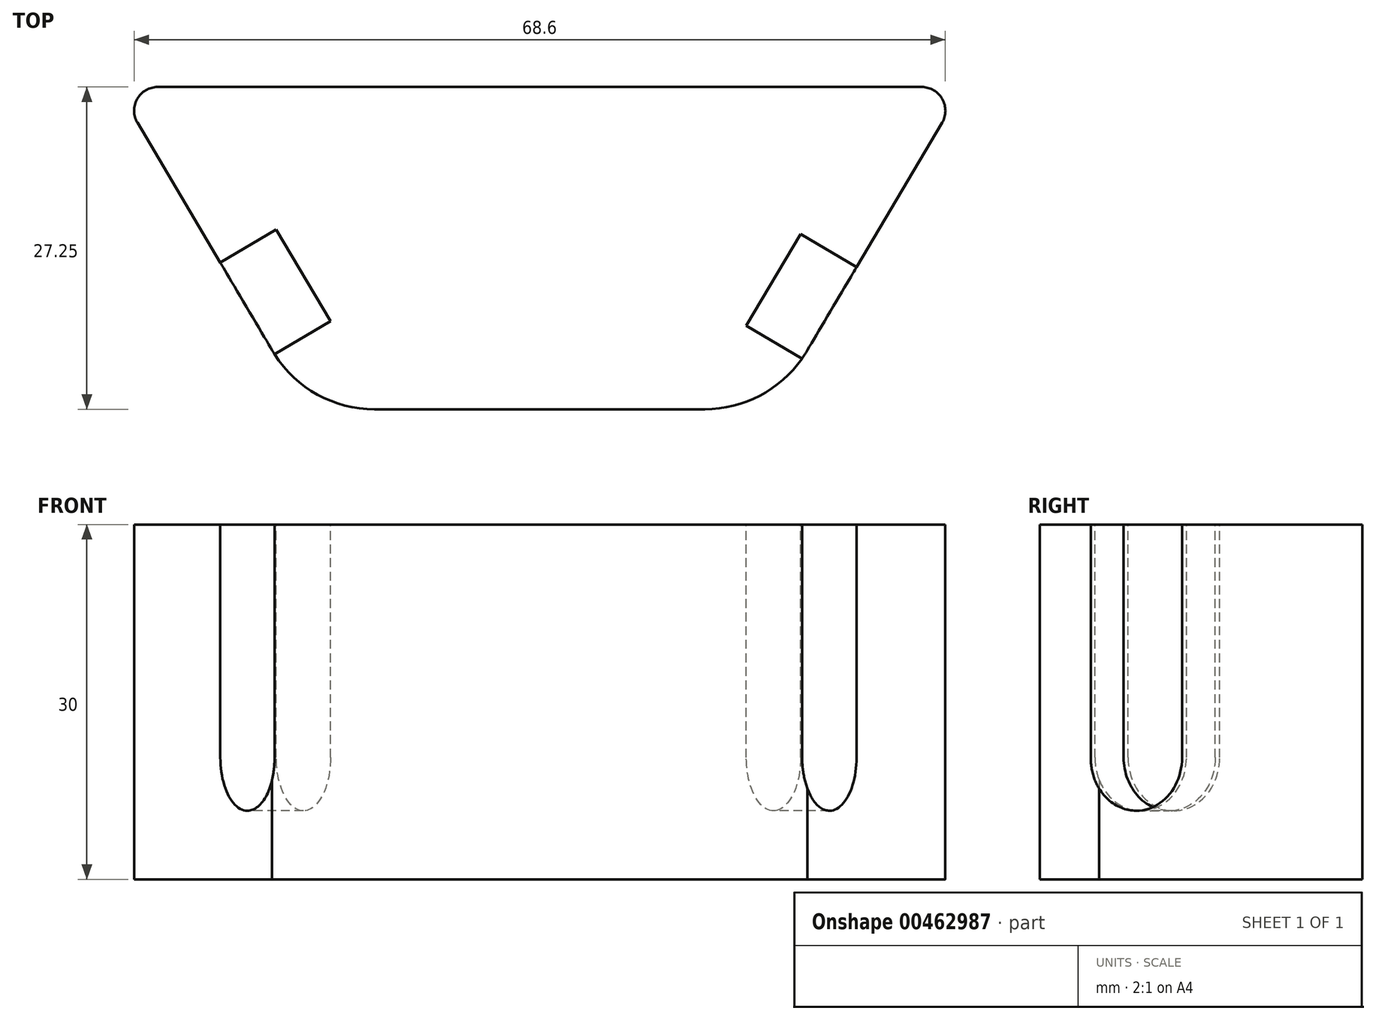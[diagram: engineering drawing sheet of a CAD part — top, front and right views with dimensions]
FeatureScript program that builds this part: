
annotation { "Feature Type Name" : "Feature", "Feature Type Description" : "" }
export const myFeature = defineFeature(function(context is Context, id is Id, definition is map)
    precondition{}
    {
        {
            var Q0;
            Q0=qCreatedBy(makeId("Top.planeOp"),FACE);
            var sketch = newSketch(context, id + "F0", { "sketchPlane" : qUnion([Q0])});
            skLineSegment(sketch, "E0", {"start": v(14.22, 4.24) * mm, "end": v(-13.72, 4.24) * mm});
            skPoint(sketch, "E1.visualSharp", {"position": v(-20, 4.24) * mm});
            skArc(sketch, "E1.filletArc", {"start": v(-22.38, 9.24) * mm, "mid": v(-18.72, 5.58) * mm, "end": v(-13.72, 4.24) * mm});
            skPoint(sketch, "E2.visualSharp", {"position": v(20, 4.24) * mm});
            skArc(sketch, "E2.filletArc", {"start": v(14.22, 4.24) * mm, "mid": v(19.22, 5.58) * mm, "end": v(22.88, 9.24) * mm});
            skLineSegment(sketch, "E3", {"start": v(32.55, 31.5) * mm, "end": v(-32.05, 31.49) * mm});
            skLineSegment(sketch, "E4.trimOffspring", {"start": v(-33.77, 28.47) * mm, "end": v(-22.38, 9.24) * mm});
            skLineSegment(sketch, "E5.trimOffspring", {"start": v(34.27, 28.47) * mm, "end": v(22.88, 9.24) * mm});
            skArc(sketch, "E6.filletArc", {"start": v(-32.05, 31.49) * mm, "mid": v(-33.8, 30.48) * mm, "end": v(-33.77, 28.47) * mm});
            skPoint(sketch, "E7.visualSharp", {"position": v(36.06, 31.5) * mm});
            skArc(sketch, "E7.filletArc", {"start": v(34.27, 28.47) * mm, "mid": v(34.3, 30.48) * mm, "end": v(32.55, 31.5) * mm});
            skSolve(sketch);
        }
        {
            var Q0;
            Q0 = qSketchRegion(id + "F0", true);
            extrude(context, id + "F1", {"entities" : qUnion([Q0]), "depth" : 30 * mm, "offsetDistance" : 25 * mm});
        }
        {
            var Q0;
            Q0=makeQuery(id+"F1.opExtrude","CAP_FACE",FACE,{"disambiguationData":[OSD([sQuery(id+"F0.wireOp",EDGE,"E0"),sQuery(id+"F0.wireOp",EDGE,"E1.filletArc"),sQuery(id+"F0.wireOp",EDGE,"E2.filletArc"),sQuery(id+"F0.wireOp",EDGE,"E3"),sQuery(id+"F0.wireOp",EDGE,"E4.trimOffspring"),sQuery(id+"F0.wireOp",EDGE,"E5.trimOffspring"),sQuery(id+"F0.wireOp",EDGE,"E6.filletArc"),sQuery(id+"F0.wireOp",EDGE,"E7.filletArc")])],"isStart":false});
            var sketch = newSketch(context, id + "F2", { "sketchPlane" : qUnion([Q0])});
            skPoint(sketch, "E8.visualSharp", {"position": v(-23.46, 4.24) * mm});
            skArc(sketch, "E8.filletArc", {"start": v(-22.38, 9.24) * mm, "mid": v(-22.28, 9.06) * mm, "end": v(-22.17, 8.89) * mm});
            skPoint(sketch, "E9.visualSharp", {"position": v(16.54, 4.24) * mm});
            skArc(sketch, "E9.filletArc", {"start": v(22.43, 8.53) * mm, "mid": v(22.66, 8.88) * mm, "end": v(22.88, 9.24) * mm});
            skLineSegment(sketch, "E10", {"start": v(-17.44, 11.69) * mm, "end": v(-22.03, 19.43) * mm});
            skLineSegment(sketch, "E11", {"start": v(-22.03, 19.43) * mm, "end": v(-26.76, 16.63) * mm});
            skPoint(sketch, "E12", {"position": v(-19.42, 4.24) * mm});
            skLineSegment(sketch, "E13", {"start": v(27.04, 16.26) * mm, "end": v(22.3, 19.06) * mm});
            skLineSegment(sketch, "E14", {"start": v(22.3, 19.06) * mm, "end": v(17.72, 11.32) * mm});
            skLineSegment(sketch, "E15", {"start": v(-17.44, 11.69) * mm, "end": v(-22.17, 8.89) * mm});
            skLineSegment(sketch, "E16", {"start": v(17.72, 11.32) * mm, "end": v(22.43, 8.53) * mm});
            skPoint(sketch, "E17.orphan", {"position": v(-13.72, 4.24) * mm});
            skPoint(sketch, "E18.orphan", {"position": v(14.22, 4.24) * mm});
            skLineSegment(sketch, "E19", {"start": v(22.88, 9.24) * mm, "end": v(27.04, 16.26) * mm});
            skLineSegment(sketch, "E20", {"start": v(-26.76, 16.63) * mm, "end": v(-22.38, 9.24) * mm});
            skSolve(sketch);
        }
        {
            var Q0;
            Q0 = qSketchRegion(id + "F2", true);
            extrude(context, id + "F3", {"entities" : qUnion([Q0]), "operationType" : NewBodyOperationType.REMOVE, "oppositeDirection" : true, "depth" : 24.2 * mm, "offsetDistance" : 25 * mm});
        }
        {
            var Q0;
            Q0=makeQuery(id+"F3.boolean.opBoolean","COPY",EDGE,{"derivedFrom":makeQuery(id+"F3.opExtrude","CAP_EDGE",EDGE,{"disambiguationData":[OSD([sQuery(id+"F2.wireOp",EDGE,"E11")])],"isStart":false})});
            var Q1;
            Q1=makeQuery(id+"F3.boolean.opBoolean","COPY",EDGE,{"derivedFrom":makeQuery(id+"F3.opExtrude","CAP_EDGE",EDGE,{"disambiguationData":[OSD([sQuery(id+"F2.wireOp",EDGE,"E15")])],"isStart":false})});
            var Q2;
            Q2=makeQuery(id+"F3.boolean.opBoolean","COPY",EDGE,{"derivedFrom":makeQuery(id+"F3.opExtrude","CAP_EDGE",EDGE,{"disambiguationData":[OSD([sQuery(id+"F2.wireOp",EDGE,"E13")])],"isStart":false})});
            var Q3;
            Q3=makeQuery(id+"F3.boolean.opBoolean","COPY",EDGE,{"derivedFrom":makeQuery(id+"F3.opExtrude","CAP_EDGE",EDGE,{"disambiguationData":[OSD([sQuery(id+"F2.wireOp",EDGE,"E16")])],"isStart":false})});
            fillet(context, id + "F4", {"entities" : qUnion([Q0, Q1, Q2, Q3]), "radius" : 4.5 * mm, "tangentPropagation" : true, "allowEdgeOverflow" : false});
        }
    });
